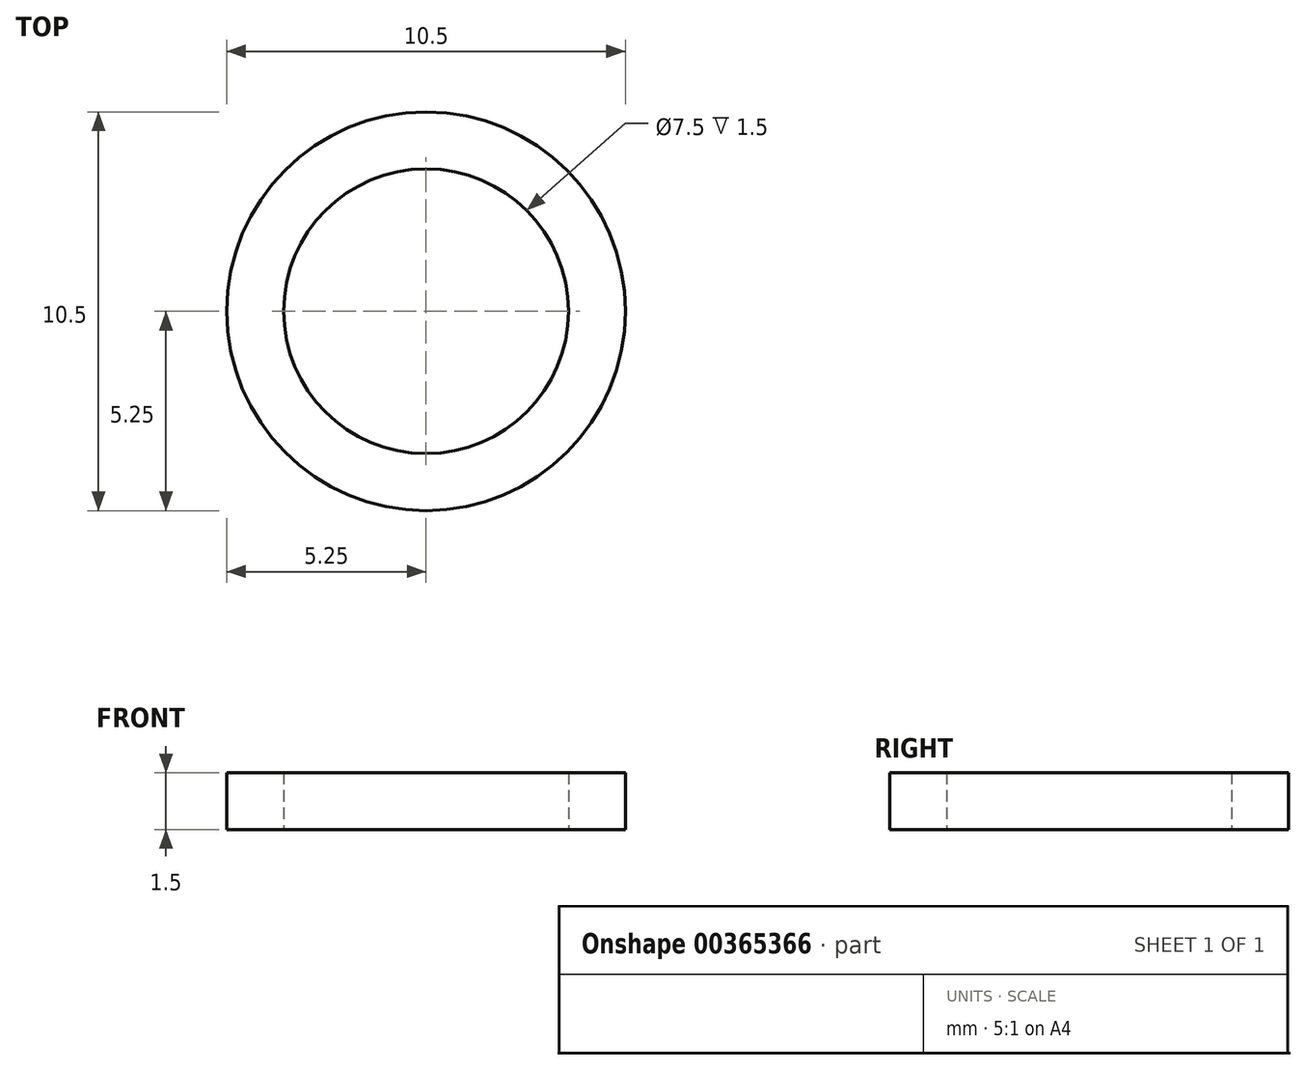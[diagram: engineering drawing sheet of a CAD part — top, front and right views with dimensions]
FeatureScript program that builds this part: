
annotation { "Feature Type Name" : "Feature", "Feature Type Description" : "" }
export const myFeature = defineFeature(function(context is Context, id is Id, definition is map)
    precondition{}
    {
        {
            var Q0;
            Q0=qCreatedBy(makeId("Top.planeOp"),FACE);
            var sketch = newSketch(context, id + "F0", { "sketchPlane" : qUnion([Q0])});
            skCircle(sketch, "E0", {"center": v(0, 0) * mm, "radius": 5.25 * mm});
            skCircle(sketch, "E1", {"center": v(0, 0) * mm, "radius": 3.75 * mm});
            skSolve(sketch);
        }
        {
            var Q0;
            Q0=qSketchRegion(id+"F0",true);
            extrude(context, id + "F1", {"entities" : qUnion([Q0]), "depth" : 1.5 * mm});
        }
    });
